# Revit family: Drinking_Fountain-Wall_Mounted-Murdock_Mfg-A171-UG-VR
name_source: partatom
category: Plumbing Fixtures
units: mm (PartAtom-declared; Revit-internal decimal feet)

## family parameters
Cut with Voids When Loaded = Yes
Host = Face
OmniClass Number = 23.65.70.14.11
OmniClass Title = Drinking Fountains/Coolers
Part Type = Normal
Room Calculation Point = No
Round Connector Dimension = Use Diameter
Shared = Yes

## types (1)
- A171408S-FG-VR
    -220V 220 volt / 50 Hz Compressor = No
    -CSC2 Concealed Support Carrier = No
    -WB1 Wall Bezel, Stainless Steel = No
    -WF1 1500-Gallon Capacity, NSF 42+53, 1 micron Lead Reduction Filter = No
    ADA Compliant = Yes
    Activation = Push Button
    Assembly Code = D2010820
    CW Connection = Yes
    CWFU = 1.5
    Cold Water Connection Diameter = 3/8"
    Cold Water Connection Height = 22 1/4"
    Cold Water Connection Width = 6 1/2"
    Compliance Certifications = AHRI Standard 1010, ANSI A117.1, NSF/ANSI 61, Section 9, UL Listed (US and Canada), Green cUPC Water Efficiency
    Default Elevation = 0"
    Description = 14GA Stainless Steel, Vandal-Resistant, Wall-Mounted Drinking Fountain - In-Unit Refrigeration (8GPH), ADA
    Finish = Stainless Steel-Murdock-Satin
    Finish- Push Button = Brass-Murdock-Chrome Plated
    Finish-Bubbler = Stainless Steel-Murdock-Polished
    Full Load Amps = 4 A
    GPH Value = 8.0
    HW Connection = No
    HWFU = 1.5
    Height = 19 3/8"
    Installation Type = Wall Mounted
    Length = 18 1/2"
    Manufacturer = Murdock Manufacturing
    Material = Stainless Steel-Murdock-Satin
    Model = A171408S-FG-VR
    Pressure Range = 20-105 psig
    Product Documentation Link = https://www.murdockmfg.com
    Product Page URL = https://www.murdockmfg.com
    Rated Watts = 335 W
    Shipping Weight = 85 lbs.
    URL = https://www.murdockmfg.com
    Vent Connection = No
    WFU = 2
    Warranty Information = Murdock Mfg.™ warrants that its products are free from defects in material or workmanship under normal use and service for a period of one year from date of shipment.
    Waste Connection = Yes
    Waste Connection Diameter = 1 1/4"
    Waste Connection Height = 22 1/4"
    Width = 18 1/2"
    cUPC Compliant = Yes

## geometry (parser evidence)
native form markers: Sweep x3
no freeform markers — native parametric forms only
